# Revit family: 434505551_Regadera Con Brazo Nogal
name_source: partatom
category: Plumbing Fixtures
units: mm (PartAtom-declared; Revit-internal decimal feet)

## family parameters
Always vertical = Yes
Cut with Voids When Loaded = No
Host = Wall
OmniClass Number = 23.31.17.00
OmniClass Title = Showers
Part Type = Normal
Room Calculation Point = No
Round Connector Dimension = Use Diameter
Shared = No

## types (1)
- Type 1
    Alto = 117 mm  [stored 0.383858 ft]
    Altura Ducha = 1500 mm  [stored 4.92126 ft]
    Ancho = 102 mm  [stored 0.334646 ft]
    Capacidad de flujo = 9,3 L/min.
    Creado por = BIMBAU
    Default Elevation = 0 mm  [stored 0 ft]
    Description = La regadera Nogal con tecnología de ahorro de agua minimiza el
derroche ofreciendo un mayor rendimiento sin sacrificar el confort en
la ducha, con chorro focalizado ofrece mayor practicidad en espacios
pequeños o consumidores que buscan cobertura direccionada.
    Fecha de creación = 09/04/2021
    Garantía = 30 Años Grival - 2 Años Cromado
    Manufacturer = Grival
    Material = Corona_Aluminio
    Material 2 = Corona_Plastico_Negro
    Model = Ducha Nogal Regadera con Brazo
    Peso neto = 150 g. - 0,33 lb.
    Presion maxima = 125 psi (860 kPa)
    Presion minima = 20 psi (140 kPa).
    Profundidad = 191 mm  [stored 0.62664 ft]
    Referencia = 434505551
    URL = https://www.grival.com
    Use Temperature = 5˚C a 71˚C.
    Vida útil = 10.000 ciclos.

note: [stored X ft] marks values corroborated as IEEE doubles in the binary element streams (Revit-internal decimal feet)

## geometry (parser evidence)
native form markers: Sweep x3
no freeform markers — native parametric forms only
